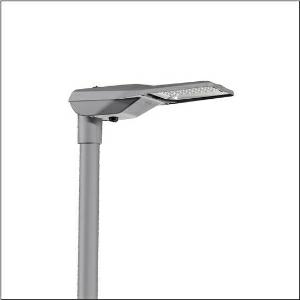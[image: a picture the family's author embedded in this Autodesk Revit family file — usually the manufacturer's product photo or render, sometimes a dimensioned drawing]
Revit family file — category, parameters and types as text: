
# Revit family: streetlight_sl_21_mini___stw1_0a_5xe2e43t08jb_eeda
name_source: partatom
category: Lighting Fixtures
units: mm (PartAtom-declared; Revit-internal decimal feet)

## family parameters
Cut with Voids When Loaded = No
Host = Face
Light Source = No
Part Type = Normal
Room Calculation Point = No
Round Connector Dimension = Use Diameter
Shared = No

## types (1)
- --- (1 x LED, 13500 lm, 88.6 W, 4000K)
    Apparent Load = 89 VA
    CIE Flux Codes = 39 75 98 100 100
    Color Rendering = 70
    Color Temperature = 4000K
    Default Elevation = 1800 mm
    Description = Streetlight SL 21 mini, mast luminaire, primary light control with lens, of PMMA, primary optical cover: cover, of toughened safety glass, transparent, light distribution: STW1.0a, light emission: direct distribution, primary light characteristic: asymmetric, installation type: side-entry, post-top, LED, High Power LED, rated luminous flux: 13.500lm, luminous efficacy: 152lm/W, light colour: 740, colour temperature: 4000K, control gear: D4i, control: overheat protection, constant luminous flux control, time-dependent luminous flux control, flexible luminous flux parameterisation, pre-setting: logarithmic dimming characteristic, mains connection: 220..240V, AC, 50/60Hz, start of lifetime: 89W, end of service life: 92W, reduction: 41W, luminaire housing, of diecast aluminium, powder-coated, Siteco® metallic grey (DB 702S), corrosivity category C5 mid according to DIN EN ISO 12944, please order mast flange separately, inclination adjustable: 0°, 5°, 10°, 15°, sealing non-destructively replaceable, multi-level sealing system, length: 628mm, width: 235mm, height: 110mm, mast flange for spigot size: 42mm (side-entry): 5XC10008XM4, 60/48mm (side-entry/post-top): 5XC10108XM2, 76/60mm (side-entry/post-top): 5XC10108XM1, mounting height: 4..8m, Smart Interface below and above, protection rating (complete): IP66, insulation class (complete): insulation class II (safety insulation), certification: CE, ENEC, ENEC+, VDE, impact resistance: IK10, permissible operating ambient temperature for outdoor applications: -40..+50°C, standard-compliant lighting for roads and squares, packaging unit: 1 piece

Light Distribution: STW1.0a
    Height = 110 mm
    Lamp = 1 x LED
    Lamp Light Flux = 13500 lm
    Lamp Power = 88.6 W
    Lamp count = 1
    Length = 625 mm
    Luminous efficacy = 152 lm/W
    Manufacturer = Siteco
    ModVariant = No
    Model = 5XE2E43T08JB
    Number of Poles = 1
    OnlyDefault = Yes
    Power Factor = 1
    Product Name = Streetlight SL 21 mini | STW1.0a
    Product group = mast luminaire | pylon top
    ProductGroupID = 6100
    Protection Class = Protection class II
    Protection Degree = IP 66
    RLX_Detail_Level = 1
    RLX_Emergency_Light_Flux = 0 lm
    RLX_Emergency_Type = 0
    RLX_Emergency_Type_DB = No
    RlxData = <blob elided: 26457 chars, md5=14627961>
    Socket = socket
    Standby Power = 0 W
    System Light Flux = 13500 lm
    System Power = 89 W
    Type Comments = factory setting: luminous flux: 100 % | dim-lin: 254 | 915 mA
    Type Image = l_1003514.jpg
    URL = http://relux.com
    VarID = @adj_031401
    Voltage = 0 V
    Weight = 0.00 kg
    Width = 234 mm

## geometry (parser evidence)
native form markers: Blend x4, Sweep x10
no freeform markers — native parametric forms only
